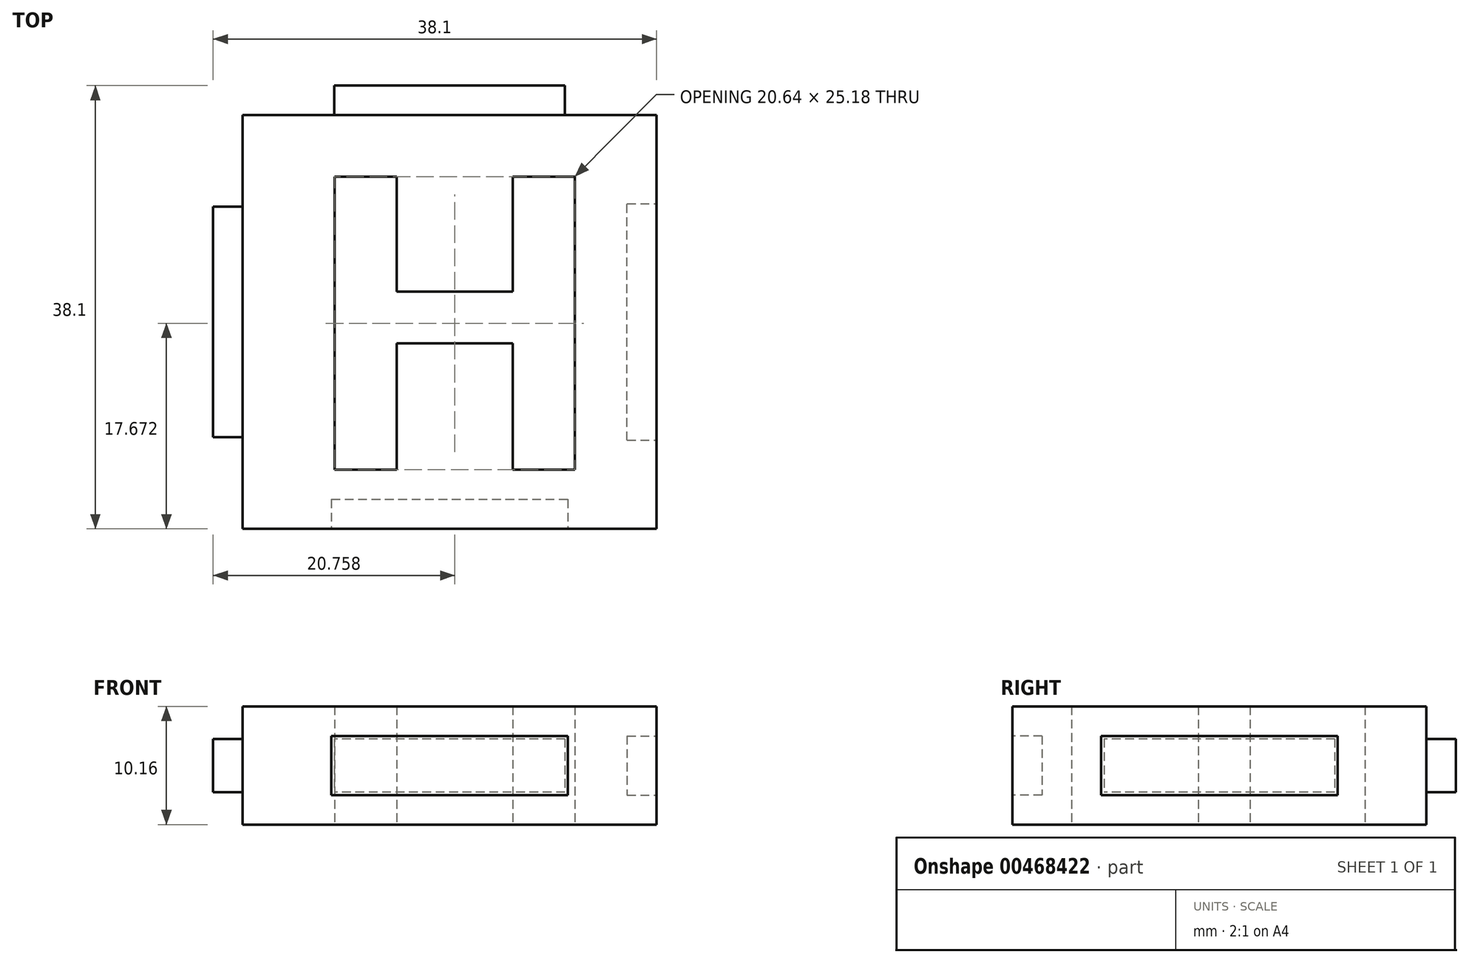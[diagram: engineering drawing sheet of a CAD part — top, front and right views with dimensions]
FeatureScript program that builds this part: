
annotation { "Feature Type Name" : "Feature", "Feature Type Description" : "" }
export const myFeature = defineFeature(function(context is Context, id is Id, definition is map)
    precondition{}
    {
        {
            var Q0;
            Q0=qCreatedBy(makeId("Top.planeOp"),FACE);
            var sketch = newSketch(context, id + "F0", { "sketchPlane" : qUnion([Q0])});
            skLineSegment(sketch, "E0.bottom", {"start": v(-17.78, 17.78) * mm, "end": v(17.78, 17.78) * mm});
            skLineSegment(sketch, "E0.top", {"start": v(-17.78, -17.78) * mm, "end": v(17.78, -17.78) * mm});
            skLineSegment(sketch, "E0.left", {"start": v(-17.78, 17.78) * mm, "end": v(-17.78, -17.78) * mm});
            skLineSegment(sketch, "E0.right", {"start": v(17.78, 17.78) * mm, "end": v(17.78, -17.78) * mm});
            skText(sketch, "E1", { "text": "H", "fontName": "OpenSans-Bold.ttf"});
            const initialGuessF0  = {"E1": [-0.01305, -0.0127, 1, 0, 0.0254]};
            skSetInitialGuess(sketch, initialGuessF0);
            skSolve(sketch);
        }
        {
            var Q0;
            Q0=qSketchRegion(id+"F0",true);
            extrude(context, id + "F1", {"entities" : qUnion([Q0]), "endBound" : BoundingType.SYMMETRIC, "depth" : 10.16 * mm});
        }
        {
            var Q0;
            Q0=makeQuery(id+"F1.opExtrude","SWEPT_FACE",FACE,{"disambiguationData":[OSD([sQuery(id+"F0.wireOp",EDGE,"E0.bottom")])]});
            var sketch = newSketch(context, id + "F2", { "sketchPlane" : qUnion([Q0])});
            skLineSegment(sketch, "E2.bottom", {"start": v(-9.9, 2.29) * mm, "end": v(9.9, 2.29) * mm});
            skLineSegment(sketch, "E2.top", {"start": v(-9.9, -2.29) * mm, "end": v(9.9, -2.29) * mm});
            skLineSegment(sketch, "E2.left", {"start": v(-9.9, 2.29) * mm, "end": v(-9.9, -2.29) * mm});
            skLineSegment(sketch, "E2.right", {"start": v(9.9, 2.29) * mm, "end": v(9.9, -2.29) * mm});
            skSolve(sketch);
        }
        {
            var Q0;
            Q0=qSketchRegion(id+"F2",true);
            extrude(context, id + "F3", {"entities" : qUnion([Q0]), "operationType" : NewBodyOperationType.ADD, "depth" : 2.54 * mm});
        }
        {
            var Q0;
            Q0=makeQuery(id+"F1.opExtrude","SWEPT_FACE",FACE,{"disambiguationData":[OSD([sQuery(id+"F0.wireOp",EDGE,"E0.left")])]});
            var sketch = newSketch(context, id + "F4", { "sketchPlane" : qUnion([Q0])});
            skLineSegment(sketch, "E3.bottom", {"start": v(-9.9, 2.29) * mm, "end": v(9.9, 2.29) * mm});
            skLineSegment(sketch, "E3.top", {"start": v(-9.9, -2.29) * mm, "end": v(9.9, -2.29) * mm});
            skLineSegment(sketch, "E3.left", {"start": v(-9.9, 2.29) * mm, "end": v(-9.9, -2.29) * mm});
            skLineSegment(sketch, "E3.right", {"start": v(9.9, 2.29) * mm, "end": v(9.9, -2.29) * mm});
            skSolve(sketch);
        }
        {
            var Q0;
            Q0=qSketchRegion(id+"F4",true);
            extrude(context, id + "F5", {"entities" : qUnion([Q0]), "operationType" : NewBodyOperationType.ADD, "depth" : 2.54 * mm});
        }
        {
            var Q0;
            Q0=makeQuery(id+"F1.opExtrude","SWEPT_FACE",FACE,{"disambiguationData":[OSD([sQuery(id+"F0.wireOp",EDGE,"E0.top")])]});
            var sketch = newSketch(context, id + "F6", { "sketchPlane" : qUnion([Q0])});
            skLineSegment(sketch, "E4.bottom", {"start": v(-10.16, 2.54) * mm, "end": v(10.16, 2.54) * mm});
            skLineSegment(sketch, "E4.top", {"start": v(-10.16, -2.54) * mm, "end": v(10.16, -2.54) * mm});
            skLineSegment(sketch, "E4.left", {"start": v(-10.16, 2.54) * mm, "end": v(-10.16, -2.54) * mm});
            skLineSegment(sketch, "E4.right", {"start": v(10.16, 2.54) * mm, "end": v(10.16, -2.54) * mm});
            skSolve(sketch);
        }
        {
            var Q0;
            Q0=qSketchRegion(id+"F6",true);
            extrude(context, id + "F7", {"entities" : qUnion([Q0]), "operationType" : NewBodyOperationType.REMOVE, "oppositeDirection" : true, "depth" : 2.54 * mm});
        }
        {
            var Q0;
            Q0=makeQuery(id+"F1.opExtrude","SWEPT_FACE",FACE,{"disambiguationData":[OSD([sQuery(id+"F0.wireOp",EDGE,"E0.right")])]});
            var sketch = newSketch(context, id + "F8", { "sketchPlane" : qUnion([Q0])});
            skLineSegment(sketch, "E5.bottom", {"start": v(-10.16, 2.54) * mm, "end": v(10.16, 2.54) * mm});
            skLineSegment(sketch, "E5.top", {"start": v(-10.16, -2.54) * mm, "end": v(10.16, -2.54) * mm});
            skLineSegment(sketch, "E5.left", {"start": v(-10.16, 2.54) * mm, "end": v(-10.16, -2.54) * mm});
            skLineSegment(sketch, "E5.right", {"start": v(10.16, 2.54) * mm, "end": v(10.16, -2.54) * mm});
            skSolve(sketch);
        }
        {
            var Q0;
            Q0=qSketchRegion(id+"F8",true);
            extrude(context, id + "F9", {"entities" : qUnion([Q0]), "operationType" : NewBodyOperationType.REMOVE, "oppositeDirection" : true, "depth" : 2.54 * mm});
        }
    });
